# Revit family: WALL WASHER HIGH POWER LED 100CM_LK2036WW.30_CW.30
name_source: partatom
category: Luminarias
units: mm (PartAtom-declared; Revit-internal decimal feet)

## family parameters
Compartido = No
Corte con vacíos al cargar = No
Cota de conector redondo = Diámetro de uso
Origen de luz = Sí
Punto de cálculo de habitación = No
Se basa en plano de trabajo = Sí
Siempre vertical = No
Tipo de pieza = Normal

## types (2) — shared parameters
Archivo de red fotométrica = LK2036WW.IES
Cambio de temperatura de color de luz atenuada = Curva de lámpara incandescente
Comentarios de vataje = 100-277V
Fabricante = BRILLANT
Filtro de color = 16777215
Longitud de línea de emisión = 400 mm  [stored 1.31234 ft]
Lámpara = OSRAM
Watt per fixture = 41
Ángulo de inclinación = 60.00°
zero-valued in all types: Elevación por defecto

## per-type parameters (varying)
| type | Descripción | Modelo |
| REFL_LK2036WW.30 | LUMINARIA TIPO REFLECTOR LINEAL, WALL WASHER , CUERPO DE ALUMINIO EXTRUIDO CON POLVO GRIS, VIDRIO TEMPLADO DE 3MM ADEMAS DEL SELLADO CON SILICON EN VIDRIO Y HOUSING, CUENTA CON 20 LED TIPO OSRAM CON UN CONSUMO TOTAL DE 41W, 2518 LUMENES, CON UNA TEMPERATURA EN BLANCO CALIDO A 3000K, IP 66, IRC 80, IK 05, CABLE H05RN DE 0.5M, APERTURA DE 30 GRADOS EN STOCK, ALIMENTADA CON FUENTE REMOTA A 100-277V. | LK2036WW.30 |
| REFL_LK2036CW.30 | LUMINARIA TIPO REFLECTOR LINEAL, WALL WASHER , CUERPO DE ALUMINIO EXTRUIDO CON POLVO GRIS, VIDRIO TEMPLADO DE 3MM ADEMAS DEL SELLADO CON SILICON EN VIDRIO Y HOUSING, CUENTA CON 20 LED TIPO OSRAM CON UN CONSUMO TOTAL DE 41W, 2890 LUMENES, CON UNA TEMPERATURA EN BLANCO FRIO A 6000K, IP 66, IRC 80, IK 05, CABLE H05RN DE 0.5M, APERTURA DE 30 GRADOS EN STOCK, ALIMENTADA CON FUENTE REMOTA A 100-277V. | LK2036CW.30 |

note: [stored X ft] marks values corroborated as IEEE doubles in the binary element streams (Revit-internal decimal feet)

## geometry (parser evidence)
native form markers: Blend x2
no freeform markers — native parametric forms only
